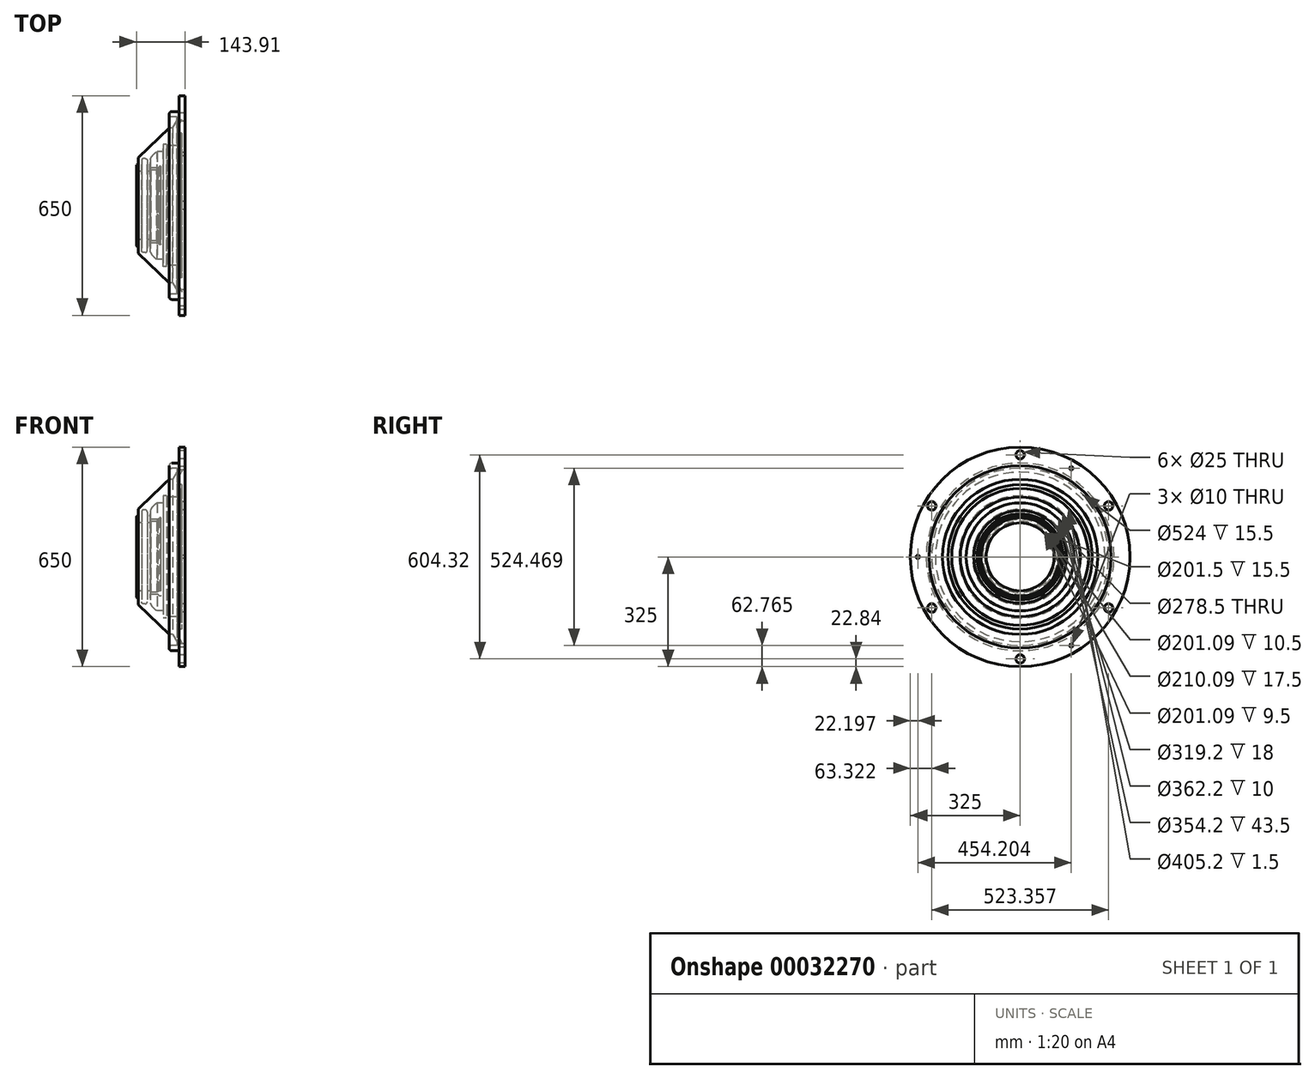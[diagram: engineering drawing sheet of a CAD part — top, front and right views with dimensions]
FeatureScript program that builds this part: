
annotation { "Feature Type Name" : "Feature", "Feature Type Description" : "" }
export const myFeature = defineFeature(function(context is Context, id is Id, definition is map)
    precondition{}
    {
        {
            var Q0;
            Q0=qCreatedBy(makeId("Front.planeOp"),FACE);
            var sketch = newSketch(context, id + "F0", { "sketchPlane" : qUnion([Q0])});
            skLineSegment(sketch, "E0", {"start": v(-1319.7, 0) * mm, "end": v(1394.77, 0) * mm, "construction": true});
            skLineSegment(sketch, "E1", {"start": v(0, 0) * mm, "end": v(0, 325) * mm, "construction": true});
            skLineSegment(sketch, "E2", {"start": v(0, 325) * mm, "end": v(-17.5, 325) * mm});
            skLineSegment(sketch, "E3", {"start": v(-17.5, 325) * mm, "end": v(-17.5, 278) * mm});
            skLineSegment(sketch, "E4", {"start": v(-17.5, 278) * mm, "end": v(-39, 278) * mm});
            skLineSegment(sketch, "E5", {"start": v(-47, 270) * mm, "end": v(-47, 270) * mm});
            skPoint(sketch, "E6.visualSharp", {"position": v(-47, 278) * mm});
            skArc(sketch, "E6.filletArc", {"start": v(-39, 278) * mm, "mid": v(-44.66, 275.66) * mm, "end": v(-47, 270) * mm});
            skLineSegment(sketch, "E7", {"start": v(-39, 262) * mm, "end": v(-23.5, 262) * mm});
            skPoint(sketch, "E8.visualSharp", {"position": v(-47, 262) * mm});
            skArc(sketch, "E8.filletArc", {"start": v(-47, 270) * mm, "mid": v(-44.66, 264.34) * mm, "end": v(-39, 262) * mm});
            skLineSegment(sketch, "E9", {"start": v(-23.5, 262) * mm, "end": v(-23.5, 251) * mm});
            skLineSegment(sketch, "E10", {"start": v(-23.5, 251) * mm, "end": v(-36.25, 228.92) * mm});
            skLineSegment(sketch, "E11", {"start": v(-36.25, 228.92) * mm, "end": v(-47.25, 228.92) * mm});
            skLineSegment(sketch, "E12", {"start": v(-47.25, 228.92) * mm, "end": v(-138.41, 141.21) * mm});
            skLineSegment(sketch, "E13", {"start": v(-138.41, 141.21) * mm, "end": v(-138.41, 123.21) * mm});
            skLineSegment(sketch, "E14", {"start": v(-138.41, 123.21) * mm, "end": v(-143.91, 119.75) * mm});
            skLineSegment(sketch, "E15", {"start": v(-143.91, 119.75) * mm, "end": v(-143.91, 100.75) * mm});
            skLineSegment(sketch, "E16", {"start": v(-143.91, 100.75) * mm, "end": v(-128.41, 100.75) * mm});
            skLineSegment(sketch, "E17", {"start": v(-128.41, 100.75) * mm, "end": v(-128.41, 133.25) * mm});
            skLineSegment(sketch, "E18", {"start": v(-122.41, 139.25) * mm, "end": v(-117.91, 139.25) * mm});
            skPoint(sketch, "E19.visualSharp", {"position": v(-128.41, 139.25) * mm});
            skArc(sketch, "E19.filletArc", {"start": v(-122.41, 139.25) * mm, "mid": v(-126.65, 137.5) * mm, "end": v(-128.41, 133.25) * mm});
            skLineSegment(sketch, "E20", {"start": v(-111.91, 133.25) * mm, "end": v(-111.91, 100.54) * mm});
            skPoint(sketch, "E21.visualSharp", {"position": v(-111.91, 139.25) * mm});
            skArc(sketch, "E21.filletArc", {"start": v(-111.91, 133.25) * mm, "mid": v(-113.67, 137.5) * mm, "end": v(-117.91, 139.25) * mm});
            skLineSegment(sketch, "E22", {"start": v(-111.91, 100.54) * mm, "end": v(-101.41, 100.54) * mm});
            skLineSegment(sketch, "E23", {"start": v(-101.41, 100.54) * mm, "end": v(-101.41, 105.04) * mm});
            skLineSegment(sketch, "E24", {"start": v(-101.41, 105.04) * mm, "end": v(-83.91, 105.04) * mm});
            skLineSegment(sketch, "E25", {"start": v(-83.91, 105.04) * mm, "end": v(-81.37, 100.54) * mm});
            skLineSegment(sketch, "E26", {"start": v(-81.37, 100.54) * mm, "end": v(-71.87, 100.54) * mm});
            skLineSegment(sketch, "E27", {"start": v(-71.87, 100.54) * mm, "end": v(-71.87, 116.04) * mm});
            skLineSegment(sketch, "E28", {"start": v(-71.87, 116.04) * mm, "end": v(-74.37, 116.04) * mm});
            skLineSegment(sketch, "E29", {"start": v(-74.37, 116.04) * mm, "end": v(-79.26, 111.04) * mm});
            skLineSegment(sketch, "E30", {"start": v(-79.26, 111.04) * mm, "end": v(-96.26, 111.04) * mm});
            skLineSegment(sketch, "E31", {"start": v(-96.26, 111.04) * mm, "end": v(-99.76, 111.04) * mm});
            skLineSegment(sketch, "E32", {"start": v(-103.76, 115.04) * mm, "end": v(-103.76, 120.54) * mm});
            skPoint(sketch, "E33.visualSharp", {"position": v(-103.76, 111.04) * mm});
            skArc(sketch, "E33.filletArc", {"start": v(-103.76, 115.04) * mm, "mid": v(-102.6, 112.21) * mm, "end": v(-99.76, 111.04) * mm});
            skLineSegment(sketch, "E34", {"start": v(-103.76, 120.54) * mm, "end": v(-102.94, 127.5) * mm});
            skLineSegment(sketch, "E35", {"start": v(-102.94, 127.5) * mm, "end": v(-102.94, 137) * mm});
            skLineSegment(sketch, "E36", {"start": v(-71.87, 116.04) * mm, "end": v(-56.87, 116.04) * mm, "construction": true});
            skArc(sketch, "E37", {"start": v(-82.64, 159.6) * mm, "mid": v(-94.53, 149.86) * mm, "end": v(-102.94, 137) * mm});
            skPoint(sketch, "E38.start.orphan", {"position": v(-82.64, 102.8) * mm});
            skLineSegment(sketch, "E39", {"start": v(-82.64, 159.6) * mm, "end": v(-64.64, 159.6) * mm});
            skLineSegment(sketch, "E40", {"start": v(-64.64, 159.6) * mm, "end": v(-64.64, 181.1) * mm});
            skLineSegment(sketch, "E41", {"start": v(-64.64, 181.1) * mm, "end": v(-54.64, 181.1) * mm});
            skLineSegment(sketch, "E42", {"start": v(-54.64, 181.1) * mm, "end": v(-54.64, 177.1) * mm});
            skLineSegment(sketch, "E43", {"start": v(-54.64, 177.1) * mm, "end": v(-11.14, 177.1) * mm});
            skLineSegment(sketch, "E44", {"start": v(-11.14, 177.1) * mm, "end": v(-11.14, 202.6) * mm});
            skLineSegment(sketch, "E45", {"start": v(-11.14, 202.6) * mm, "end": v(-9.64, 202.6) * mm});
            skLineSegment(sketch, "E46", {"start": v(-9.64, 202.6) * mm, "end": v(-9.64, 213.6) * mm});
            skLineSegment(sketch, "E47", {"start": v(-9.64, 213.6) * mm, "end": v(-16.14, 213.6) * mm});
            skLineSegment(sketch, "E48", {"start": v(-16.14, 213.6) * mm, "end": v(-16.14, 213.6) * mm});
            skLineSegment(sketch, "E49", {"start": v(-23.14, 220.6) * mm, "end": v(-23.14, 220.6) * mm});
            skPoint(sketch, "E50.visualSharp", {"position": v(-23.14, 213.6) * mm});
            skArc(sketch, "E50.filletArc", {"start": v(-23.14, 220.6) * mm, "mid": v(-21.09, 215.65) * mm, "end": v(-16.14, 213.6) * mm});
            skLineSegment(sketch, "E51", {"start": v(-23.14, 220.6) * mm, "end": v(-23.14, 229.6) * mm});
            skLineSegment(sketch, "E52", {"start": v(-23.14, 229.6) * mm, "end": v(0, 269.67) * mm});
            skLineSegment(sketch, "E53", {"start": v(0, 325) * mm, "end": v(0, 269.67) * mm});
            skSolve(sketch);
        }
        {
            var Q0;
            Q0 = qSketchRegion(id + "F0", true);
            var Q1;
            Q1=sQuery(id+"F0.wireOp",EDGE,"E0");
            revolve(context, id + "F1", {"entities" : qUnion([Q0]), "axis" : qUnion([Q1]), "revolveType" : RevolveType.FULL});
        }
        {
            var Q0;
            Q0=makeQuery(id+"F1.opRevolve","SWEPT_FACE",FACE,{"disambiguationData":[OSD([sQuery(id+"F0.wireOp",EDGE,"E3")])]});
            var sketch = newSketch(context, id + "F2", { "sketchPlane" : qUnion([Q0])});
            skCircle(sketch, "E54", {"center": v(0, 302.16) * mm, "radius": 12.5 * mm});
            skCircle(sketch, "E55.1.0", {"center": v(-261.68, 151.08) * mm, "radius": 12.5 * mm});
            skCircle(sketch, "E55.2.0", {"center": v(-261.68, -151.08) * mm, "radius": 12.5 * mm});
            skCircle(sketch, "E55.3.0", {"center": v(0, -302.16) * mm, "radius": 12.5 * mm});
            skCircle(sketch, "E55.4.0", {"center": v(261.68, -151.08) * mm, "radius": 12.5 * mm});
            skCircle(sketch, "E55.5.0", {"center": v(261.68, 151.08) * mm, "radius": 12.5 * mm});
            skPoint(sketch, "E55.center", {"position": v(0, 0) * mm});
            skCircle(sketch, "E56", {"center": v(297.2, 0) * mm, "radius": 5 * mm});
            skCircle(sketch, "E57.1.0", {"center": v(-148.6, 257.39) * mm, "radius": 5 * mm});
            skCircle(sketch, "E57.2.0", {"center": v(-148.6, -257.39) * mm, "radius": 5 * mm});
            skSolve(sketch);
        }
        {
            var Q0;
            Q0=sQuery(id+"F2.wireOp",VERTEX,"E54.center");
            var Q1;
            Q1=sQuery(id+"F2.wireOp",VERTEX,"E55.1.0.center");
            var Q2;
            Q2=sQuery(id+"F2.wireOp",VERTEX,"E55.5.0.center");
            var Q3;
            Q3=sQuery(id+"F2.wireOp",VERTEX,"E55.4.0.center");
            var Q4;
            Q4=sQuery(id+"F2.wireOp",VERTEX,"E55.3.0.center");
            var Q5;
            Q5=sQuery(id+"F2.wireOp",VERTEX,"E55.2.0.center");
            var Q6;
            Q6=makeQuery(id+"F1.opRevolve","SWEPT_BODY",BODY,{"disambiguationData":[OSD([sQuery(id+"F0.wireOp",EDGE,"E2"),sQuery(id+"F0.wireOp",EDGE,"E3"),sQuery(id+"F0.wireOp",EDGE,"E4"),sQuery(id+"F0.wireOp",EDGE,"E6.filletArc"),sQuery(id+"F0.wireOp",EDGE,"E7"),sQuery(id+"F0.wireOp",EDGE,"E8.filletArc"),sQuery(id+"F0.wireOp",EDGE,"E9"),sQuery(id+"F0.wireOp",EDGE,"E10"),sQuery(id+"F0.wireOp",EDGE,"E11"),sQuery(id+"F0.wireOp",EDGE,"E12"),sQuery(id+"F0.wireOp",EDGE,"E13"),sQuery(id+"F0.wireOp",EDGE,"E14"),sQuery(id+"F0.wireOp",EDGE,"E15"),sQuery(id+"F0.wireOp",EDGE,"E16"),sQuery(id+"F0.wireOp",EDGE,"E17"),sQuery(id+"F0.wireOp",EDGE,"E18"),sQuery(id+"F0.wireOp",EDGE,"E19.filletArc"),sQuery(id+"F0.wireOp",EDGE,"E20"),sQuery(id+"F0.wireOp",EDGE,"E21.filletArc"),sQuery(id+"F0.wireOp",EDGE,"E22"),sQuery(id+"F0.wireOp",EDGE,"E23"),sQuery(id+"F0.wireOp",EDGE,"E24"),sQuery(id+"F0.wireOp",EDGE,"E25"),sQuery(id+"F0.wireOp",EDGE,"E26"),sQuery(id+"F0.wireOp",EDGE,"E27"),sQuery(id+"F0.wireOp",EDGE,"E28"),sQuery(id+"F0.wireOp",EDGE,"E29"),sQuery(id+"F0.wireOp",EDGE,"E30"),sQuery(id+"F0.wireOp",EDGE,"E31"),sQuery(id+"F0.wireOp",EDGE,"E32"),sQuery(id+"F0.wireOp",EDGE,"E33.filletArc"),sQuery(id+"F0.wireOp",EDGE,"E34"),sQuery(id+"F0.wireOp",EDGE,"E35"),sQuery(id+"F0.wireOp",EDGE,"E37"),sQuery(id+"F0.wireOp",EDGE,"E39"),sQuery(id+"F0.wireOp",EDGE,"E40"),sQuery(id+"F0.wireOp",EDGE,"E41"),sQuery(id+"F0.wireOp",EDGE,"E42"),sQuery(id+"F0.wireOp",EDGE,"E43"),sQuery(id+"F0.wireOp",EDGE,"E44"),sQuery(id+"F0.wireOp",EDGE,"E45"),sQuery(id+"F0.wireOp",EDGE,"E46"),sQuery(id+"F0.wireOp",EDGE,"E47"),sQuery(id+"F0.wireOp",EDGE,"E50.filletArc"),sQuery(id+"F0.wireOp",EDGE,"E51"),sQuery(id+"F0.wireOp",EDGE,"E52"),sQuery(id+"F0.wireOp",EDGE,"E53")])]});
            hole(context, id + "F3", {"style" : HoleStyle.SIMPLE, "holeDiameter" : 25 * mm, "endStyle" : HoleEndStyle.THROUGH, "locations" : qUnion([Q0, Q1, Q2, Q3, Q4, Q5]), "scope" : qUnion([Q6])});
        }
        {
            var Q0;
            Q0=makeQuery(id+"F1.opRevolve","SWEPT_FACE",FACE,{"disambiguationData":[OSD([sQuery(id+"F0.wireOp",EDGE,"E3")])]});
            var sketch = newSketch(context, id + "F4", { "sketchPlane" : qUnion([Q0])});
            skCircle(sketch, "E58", {"center": v(302.8, 0) * mm, "radius": 5 * mm});
            skCircle(sketch, "E59.1.0", {"center": v(-151.4, 262.23) * mm, "radius": 5 * mm});
            skCircle(sketch, "E59.2.0", {"center": v(-151.4, -262.23) * mm, "radius": 5 * mm});
            skPoint(sketch, "E59.center", {"position": v(0, 0) * mm});
            skSolve(sketch);
        }
        {
            var Q0;
            Q0=sQuery(id+"F4.wireOp",VERTEX,"E58.center");
            var Q1;
            Q1=sQuery(id+"F4.wireOp",VERTEX,"E59.2.0.center");
            var Q2;
            Q2=sQuery(id+"F4.wireOp",VERTEX,"E59.1.0.center");
            var Q3;
            Q3=makeQuery(id+"F1.opRevolve","SWEPT_BODY",BODY,{"disambiguationData":[OSD([sQuery(id+"F0.wireOp",EDGE,"E2"),sQuery(id+"F0.wireOp",EDGE,"E3"),sQuery(id+"F0.wireOp",EDGE,"E4"),sQuery(id+"F0.wireOp",EDGE,"E6.filletArc"),sQuery(id+"F0.wireOp",EDGE,"E7"),sQuery(id+"F0.wireOp",EDGE,"E8.filletArc"),sQuery(id+"F0.wireOp",EDGE,"E9"),sQuery(id+"F0.wireOp",EDGE,"E10"),sQuery(id+"F0.wireOp",EDGE,"E11"),sQuery(id+"F0.wireOp",EDGE,"E12"),sQuery(id+"F0.wireOp",EDGE,"E13"),sQuery(id+"F0.wireOp",EDGE,"E14"),sQuery(id+"F0.wireOp",EDGE,"E15"),sQuery(id+"F0.wireOp",EDGE,"E16"),sQuery(id+"F0.wireOp",EDGE,"E17"),sQuery(id+"F0.wireOp",EDGE,"E18"),sQuery(id+"F0.wireOp",EDGE,"E19.filletArc"),sQuery(id+"F0.wireOp",EDGE,"E20"),sQuery(id+"F0.wireOp",EDGE,"E21.filletArc"),sQuery(id+"F0.wireOp",EDGE,"E22"),sQuery(id+"F0.wireOp",EDGE,"E23"),sQuery(id+"F0.wireOp",EDGE,"E24"),sQuery(id+"F0.wireOp",EDGE,"E25"),sQuery(id+"F0.wireOp",EDGE,"E26"),sQuery(id+"F0.wireOp",EDGE,"E27"),sQuery(id+"F0.wireOp",EDGE,"E28"),sQuery(id+"F0.wireOp",EDGE,"E29"),sQuery(id+"F0.wireOp",EDGE,"E30"),sQuery(id+"F0.wireOp",EDGE,"E31"),sQuery(id+"F0.wireOp",EDGE,"E32"),sQuery(id+"F0.wireOp",EDGE,"E33.filletArc"),sQuery(id+"F0.wireOp",EDGE,"E34"),sQuery(id+"F0.wireOp",EDGE,"E35"),sQuery(id+"F0.wireOp",EDGE,"E37"),sQuery(id+"F0.wireOp",EDGE,"E39"),sQuery(id+"F0.wireOp",EDGE,"E40"),sQuery(id+"F0.wireOp",EDGE,"E41"),sQuery(id+"F0.wireOp",EDGE,"E42"),sQuery(id+"F0.wireOp",EDGE,"E43"),sQuery(id+"F0.wireOp",EDGE,"E44"),sQuery(id+"F0.wireOp",EDGE,"E45"),sQuery(id+"F0.wireOp",EDGE,"E46"),sQuery(id+"F0.wireOp",EDGE,"E47"),sQuery(id+"F0.wireOp",EDGE,"E50.filletArc"),sQuery(id+"F0.wireOp",EDGE,"E51"),sQuery(id+"F0.wireOp",EDGE,"E52"),sQuery(id+"F0.wireOp",EDGE,"E53")])]});
            hole(context, id + "F5", {"style" : HoleStyle.SIMPLE, "holeDiameter" : 10 * mm, "endStyle" : HoleEndStyle.THROUGH, "locations" : qUnion([Q0, Q1, Q2]), "scope" : qUnion([Q3])});
        }
    });
